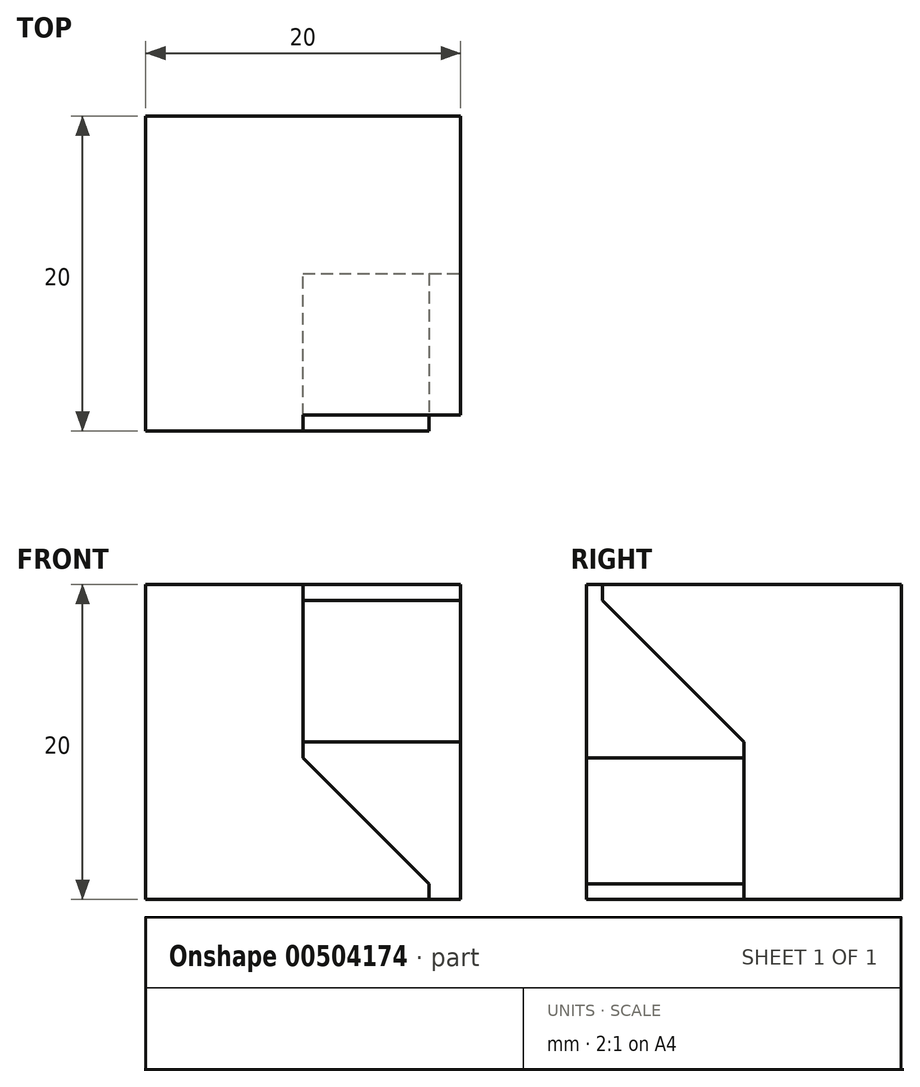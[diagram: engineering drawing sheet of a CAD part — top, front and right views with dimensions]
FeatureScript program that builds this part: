
annotation { "Feature Type Name" : "Feature", "Feature Type Description" : "" }
export const myFeature = defineFeature(function(context is Context, id is Id, definition is map)
    precondition{}
    {
        {
            var Q0;
            Q0=qCreatedBy(makeId("Top.planeOp"),FACE);
            var sketch = newSketch(context, id + "F0", { "sketchPlane" : qUnion([Q0])});
            skLineSegment(sketch, "E0.bottom", {"start": v(-10, 10) * mm, "end": v(10, 10) * mm});
            skLineSegment(sketch, "E0.top", {"start": v(-10, -10) * mm, "end": v(10, -10) * mm});
            skLineSegment(sketch, "E0.left", {"start": v(-10, 10) * mm, "end": v(-10, -10) * mm});
            skLineSegment(sketch, "E0.right", {"start": v(10, 10) * mm, "end": v(10, -10) * mm});
            skPoint(sketch, "E0.middle", {"position": v(0, 0) * mm});
            skSolve(sketch);
        }
        {
            var Q0;
            Q0 = qSketchRegion(id + "F0", true);
            extrude(context, id + "F1", {"entities" : qUnion([Q0]), "depth" : 10 * mm});
        }
        {
            var Q0;
            Q0=makeQuery(id+"F1.opExtrude","SWEPT_FACE",FACE,{"disambiguationData":[OSD([sQuery(id+"F0.wireOp",EDGE,"E0.right")])]});
            var sketch = newSketch(context, id + "F2", { "sketchPlane" : qUnion([Q0])});
            skLineSegment(sketch, "E1", {"start": v(-9, 10) * mm, "end": v(-9, 9) * mm});
            skLineSegment(sketch, "E2", {"start": v(-9, 9) * mm, "end": v(0, 0) * mm});
            skLineSegment(sketch, "E3", {"start": v(0, 0) * mm, "end": v(0, 0) * mm});
            skLineSegment(sketch, "E4", {"start": v(-9, 10) * mm, "end": v(-10, 10) * mm});
            skLineSegment(sketch, "E5", {"start": v(-10, 10) * mm, "end": v(-10, 0) * mm});
            skLineSegment(sketch, "E6", {"start": v(-10, 0) * mm, "end": v(0, 0) * mm});
            skSolve(sketch);
        }
        {
            var Q0;
            Q0 = qSketchRegion(id + "F2", true);
            extrude(context, id + "F3", {"entities" : qUnion([Q0]), "operationType" : NewBodyOperationType.REMOVE, "oppositeDirection" : true, "depth" : 10 * mm});
        }
        {
            var Q0;
            Q0 = qSketchRegion(id + "F0", true);
            extrude(context, id + "F4", {"entities" : qUnion([Q0]), "operationType" : NewBodyOperationType.ADD, "oppositeDirection" : true, "depth" : 10 * mm});
        }
        {
            var Q0;
            {var subQ0=sQuery(id+"F0.wireOp",EDGE,"E0.top");Q0=makeQuery(id+"F4.boolean.opBoolean","MERGE",FACE,{"derivedFrom":[makeQuery(id+"F1.opExtrude","SWEPT_FACE",FACE,{"disambiguationData":[OSD([subQ0])]}),makeQuery(id+"F4.opExtrude","SWEPT_FACE",FACE,{"disambiguationData":[OSD([subQ0])]})]});}
            var sketch = newSketch(context, id + "F5", { "sketchPlane" : qUnion([Q0])});
            skLineSegment(sketch, "E7", {"start": v(0, 0) * mm, "end": v(0, -1) * mm});
            skLineSegment(sketch, "E8", {"start": v(0, -1) * mm, "end": v(8, -9) * mm});
            skLineSegment(sketch, "E9", {"start": v(8, -9) * mm, "end": v(8, -10) * mm});
            skLineSegment(sketch, "E10", {"start": v(8, -10) * mm, "end": v(10, -10) * mm});
            skLineSegment(sketch, "E11", {"start": v(10, -10) * mm, "end": v(10, 0) * mm});
            skLineSegment(sketch, "E12", {"start": v(10, 0) * mm, "end": v(0, 0) * mm});
            skSolve(sketch);
        }
        {
            var Q0;
            Q0 = qSketchRegion(id + "F5", true);
            extrude(context, id + "F6", {"entities" : qUnion([Q0]), "operationType" : NewBodyOperationType.REMOVE, "oppositeDirection" : true, "depth" : 10 * mm});
        }
    });
